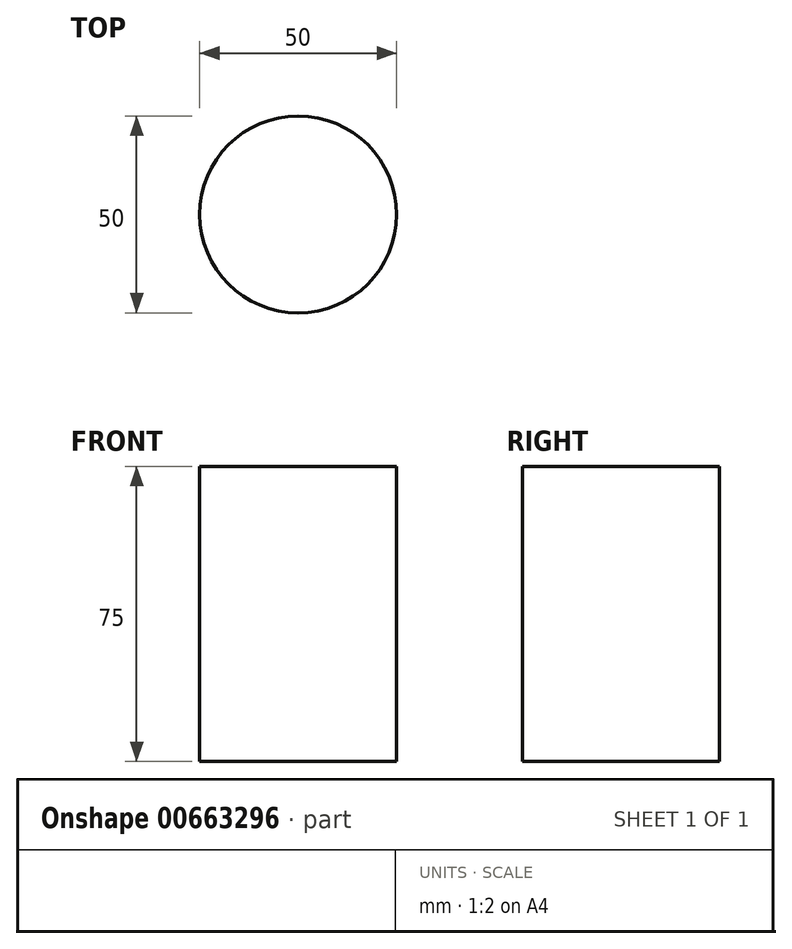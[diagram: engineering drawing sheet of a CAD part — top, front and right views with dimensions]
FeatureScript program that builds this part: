
annotation { "Feature Type Name" : "Feature", "Feature Type Description" : "" }
export const myFeature = defineFeature(function(context is Context, id is Id, definition is map)
    precondition{}
    {
        {
            var Q0;
            Q0=qCreatedBy(makeId("Top.planeOp"),FACE);
            var sketch = newSketch(context, id + "F0", { "sketchPlane" : qUnion([Q0])});
            skCircle(sketch, "E0", {"center": v(0, 0) * mm, "radius": 25 * mm});
            skSolve(sketch);
        }
        {
            var Q0;
            Q0=makeQuery(id+"F0.imprint","IMPRINT",FACE,{"disambiguationData":[TD([[makeQuery(id+"F0.imprint","IMPRINT",EDGE,{"derivedFrom":sQuery(id+"F0.wireOp",EDGE,"E0")}),1.0]])]});
            extrude(context, id + "F1", {"entities" : qUnion([Q0]), "depth" : 75 * mm, "offsetDistance" : 25 * mm});
        }
    });
